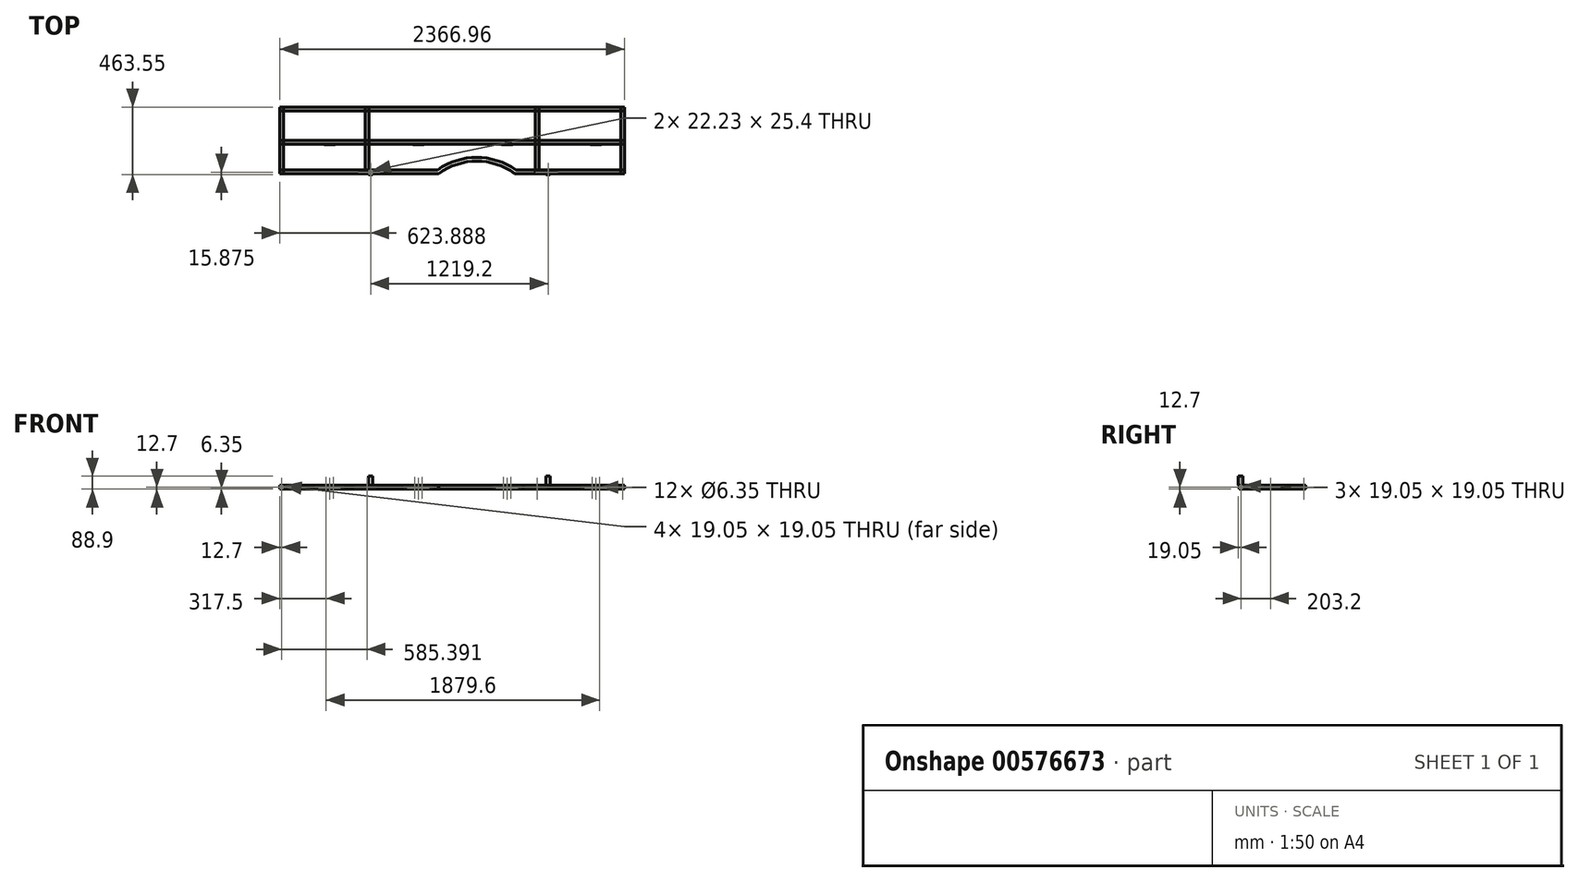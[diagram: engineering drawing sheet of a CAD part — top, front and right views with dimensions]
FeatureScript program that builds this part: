
annotation { "Feature Type Name" : "Feature", "Feature Type Description" : "" }
export const myFeature = defineFeature(function(context is Context, id is Id, definition is map)
    precondition{}
    {
        {
            var Q0;
            Q0=qCreatedBy(makeId("Top.planeOp"),FACE);
            var sketch = newSketch(context, id + "F0", { "sketchPlane" : qUnion([Q0])});
            skLineSegment(sketch, "E0", {"start": v(0, 0) * mm, "end": v(2366.96, 0) * mm});
            skLineSegment(sketch, "E1.0", {"start": v(0, 254) * mm, "end": v(2366.96, 254) * mm});
            skLineSegment(sketch, "E2.0", {"start": v(0, -203.2) * mm, "end": v(1092.2, -203.2) * mm});
            skLineSegment(sketch, "E3", {"start": v(0, 254) * mm, "end": v(0, -203.2) * mm});
            skLineSegment(sketch, "E4", {"start": v(2366.96, 254) * mm, "end": v(2366.96, -203.2) * mm});
            skLineSegment(sketch, "E5.trimOffspring", {"start": v(1612.9, -203.2) * mm, "end": v(2366.96, -203.2) * mm});
            skPoint(sketch, "E6.0.start.orphan", {"position": v(1612.9, 254) * mm});
            skPoint(sketch, "E7.orphan", {"position": v(1092.2, 254) * mm});
            skLineSegment(sketch, "E8", {"start": v(1352.55, -117.48) * mm, "end": v(1352.55, 0) * mm});
            skLineSegment(sketch, "E9.0", {"start": v(0, -117.48) * mm, "end": v(2366.96, -117.48) * mm});
            skPoint(sketch, "E10", {"position": v(1352.55, -117.48) * mm});
            skArc(sketch, "E11", {"start": v(1612.9, -203.2) * mm, "mid": v(1352.55, -117.47) * mm, "end": v(1092.2, -203.2) * mm});
            skLineSegment(sketch, "E12.0", {"start": v(279.4, 254) * mm, "end": v(279.4, -203.2) * mm, "construction": true});
            skLineSegment(sketch, "E13.0", {"start": v(711.2, 254) * mm, "end": v(711.2, -203.2) * mm, "construction": true});
            skLineSegment(sketch, "E14.0", {"start": v(1308.1, 254) * mm, "end": v(1308.1, -203.2) * mm, "construction": true});
            skLineSegment(sketch, "E15.0", {"start": v(1905, 254) * mm, "end": v(1905, -203.2) * mm, "construction": true});
            skLineSegment(sketch, "E16.0", {"start": v(2273.3, 254) * mm, "end": v(2273.3, -203.2) * mm, "construction": true});
            skLineSegment(sketch, "E17.bottom", {"start": v(279.4, 254) * mm, "end": v(335.28, 254) * mm});
            skLineSegment(sketch, "E17.top", {"start": v(279.4, 198.12) * mm, "end": v(335.28, 198.12) * mm});
            skLineSegment(sketch, "E17.left", {"start": v(279.4, 254) * mm, "end": v(279.4, 198.12) * mm});
            skLineSegment(sketch, "E17.right", {"start": v(335.28, 254) * mm, "end": v(335.28, 198.12) * mm});
            skLineSegment(sketch, "E18.bottom", {"start": v(711.2, 254) * mm, "end": v(767.08, 254) * mm});
            skLineSegment(sketch, "E18.top", {"start": v(711.2, 198.12) * mm, "end": v(767.08, 198.12) * mm});
            skLineSegment(sketch, "E18.left", {"start": v(711.2, 254) * mm, "end": v(711.2, 198.12) * mm});
            skLineSegment(sketch, "E18.right", {"start": v(767.08, 254) * mm, "end": v(767.08, 198.12) * mm});
            skLineSegment(sketch, "E19.bottom", {"start": v(1308.1, 254) * mm, "end": v(1363.98, 254) * mm});
            skLineSegment(sketch, "E19.top", {"start": v(1308.1, 198.12) * mm, "end": v(1363.98, 198.12) * mm});
            skLineSegment(sketch, "E19.left", {"start": v(1308.1, 254) * mm, "end": v(1308.1, 198.12) * mm});
            skLineSegment(sketch, "E19.right", {"start": v(1363.98, 254) * mm, "end": v(1363.98, 198.12) * mm});
            skLineSegment(sketch, "E20.bottom", {"start": v(1905, 254) * mm, "end": v(1960.88, 254) * mm});
            skLineSegment(sketch, "E20.top", {"start": v(1905, 198.12) * mm, "end": v(1960.88, 198.12) * mm});
            skLineSegment(sketch, "E20.left", {"start": v(1905, 254) * mm, "end": v(1905, 198.12) * mm});
            skLineSegment(sketch, "E20.right", {"start": v(1960.88, 254) * mm, "end": v(1960.88, 198.12) * mm});
            skLineSegment(sketch, "E21.bottom", {"start": v(2273.3, 254) * mm, "end": v(2329.18, 254) * mm});
            skLineSegment(sketch, "E21.top", {"start": v(2273.3, 198.12) * mm, "end": v(2329.18, 198.12) * mm});
            skLineSegment(sketch, "E21.left", {"start": v(2273.3, 254) * mm, "end": v(2273.3, 198.12) * mm});
            skLineSegment(sketch, "E21.right", {"start": v(2329.18, 254) * mm, "end": v(2329.18, 198.12) * mm});
            skLineSegment(sketch, "E22.0", {"start": v(254, 254) * mm, "end": v(254, -203.2) * mm});
            skLineSegment(sketch, "E23.0", {"start": v(698.5, 254) * mm, "end": v(698.5, -203.2) * mm});
            skLineSegment(sketch, "E24.0", {"start": v(1295.4, 254) * mm, "end": v(1295.4, -203.2) * mm});
            skLineSegment(sketch, "E25.0", {"start": v(1898.65, 254) * mm, "end": v(1898.65, -203.2) * mm});
            skLineSegment(sketch, "E26.0", {"start": v(2266.95, 254) * mm, "end": v(2266.95, -203.2) * mm});
            skLineSegment(sketch, "E27.bottom", {"start": v(254, 254) * mm, "end": v(309.88, 254) * mm});
            skLineSegment(sketch, "E27.top", {"start": v(254, 198.12) * mm, "end": v(309.88, 198.12) * mm});
            skLineSegment(sketch, "E27.left", {"start": v(254, 254) * mm, "end": v(254, 198.12) * mm});
            skLineSegment(sketch, "E27.right", {"start": v(309.88, 254) * mm, "end": v(309.88, 198.12) * mm});
            skLineSegment(sketch, "E28.bottom", {"start": v(698.5, 254) * mm, "end": v(749.3, 254) * mm});
            skLineSegment(sketch, "E28.top", {"start": v(698.5, 198.12) * mm, "end": v(749.3, 198.12) * mm});
            skLineSegment(sketch, "E28.left", {"start": v(698.5, 254) * mm, "end": v(698.5, 198.12) * mm});
            skLineSegment(sketch, "E28.right", {"start": v(749.3, 254) * mm, "end": v(749.3, 198.12) * mm});
            skLineSegment(sketch, "E29.bottom", {"start": v(1295.4, 254) * mm, "end": v(1351.28, 254) * mm});
            skLineSegment(sketch, "E29.top", {"start": v(1295.4, 198.12) * mm, "end": v(1351.28, 198.12) * mm});
            skLineSegment(sketch, "E29.left", {"start": v(1295.4, 254) * mm, "end": v(1295.4, 198.12) * mm});
            skLineSegment(sketch, "E29.right", {"start": v(1351.28, 254) * mm, "end": v(1351.28, 198.12) * mm});
            skLineSegment(sketch, "E30.bottom", {"start": v(1898.65, 254) * mm, "end": v(1954.53, 254) * mm});
            skLineSegment(sketch, "E30.top", {"start": v(1898.65, 198.12) * mm, "end": v(1954.53, 198.12) * mm});
            skLineSegment(sketch, "E30.left", {"start": v(1898.65, 254) * mm, "end": v(1898.65, 198.12) * mm});
            skLineSegment(sketch, "E30.right", {"start": v(1954.53, 254) * mm, "end": v(1954.53, 198.12) * mm});
            skLineSegment(sketch, "E31.bottom", {"start": v(2266.95, 254) * mm, "end": v(2322.83, 254) * mm});
            skLineSegment(sketch, "E31.top", {"start": v(2266.95, 198.12) * mm, "end": v(2322.83, 198.12) * mm});
            skLineSegment(sketch, "E31.left", {"start": v(2266.95, 254) * mm, "end": v(2266.95, 198.12) * mm});
            skLineSegment(sketch, "E31.right", {"start": v(2322.83, 254) * mm, "end": v(2322.83, 198.12) * mm});
            skLineSegment(sketch, "E32.0", {"start": v(2341.56, 254) * mm, "end": v(2341.56, -203.2) * mm, "construction": true});
            skSolve(sketch);
        }
        {
            var Q0;
            Q0=qCreatedBy(makeId("Front.planeOp"),FACE);
            cPlane(context, id + "F1", {"entities" : qUnion([Q0]), "cplaneType" : CPlaneType.OFFSET, "offset" : 203.2 * mm, "width" : 152.4 * mm, "height" : 152.4 * mm});
        }
        {
            var Q0;
            Q0=qCreatedBy(id+"F1.planeOp",FACE);
            var sketch = newSketch(context, id + "F2", { "sketchPlane" : qUnion([Q0])});
            skLineSegment(sketch, "E33.0", {"start": v(25.4, 0) * mm, "end": v(25.4, -25.4) * mm});
            skLineSegment(sketch, "E34.bottom", {"start": v(25.4, -25.4) * mm, "end": v(0, -25.4) * mm});
            skLineSegment(sketch, "E34.top", {"start": v(25.4, 0) * mm, "end": v(0, 0) * mm});
            skLineSegment(sketch, "E34.right", {"start": v(0, -25.4) * mm, "end": v(0, 0) * mm});
            skLineSegment(sketch, "E35.direction1", {"start": v(31.75, -31.75) * mm, "end": v(336.55, -31.75) * mm, "construction": true});
            skLineSegment(sketch, "E36.0", {"start": v(22.22, -3.17) * mm, "end": v(3.18, -3.18) * mm});
            skLineSegment(sketch, "E36.1", {"start": v(22.22, -3.17) * mm, "end": v(22.22, -22.23) * mm});
            skLineSegment(sketch, "E36.2", {"start": v(22.22, -22.23) * mm, "end": v(3.17, -22.23) * mm});
            skLineSegment(sketch, "E36.3", {"start": v(3.18, -22.23) * mm, "end": v(3.18, -3.18) * mm});
            skLineSegment(sketch, "E37.direction1", {"start": v(0, -25.4) * mm, "end": v(2366.96, -25.4) * mm, "construction": true});
            skLineSegment(sketch, "E38.direction1", {"start": v(0, -25.4) * mm, "end": v(609.6, -25.4) * mm, "construction": true});
            skLineSegment(sketch, "E39.1.0.0", {"start": v(610.8, -25.4) * mm, "end": v(585.4, -25.4) * mm});
            skLineSegment(sketch, "E39.1.0.1", {"start": v(585.4, -25.4) * mm, "end": v(585.4, 0) * mm});
            skLineSegment(sketch, "E39.1.0.2", {"start": v(588.57, -22.23) * mm, "end": v(588.57, -3.18) * mm});
            skLineSegment(sketch, "E39.1.0.3", {"start": v(610.8, 0) * mm, "end": v(610.8, -25.4) * mm});
            skLineSegment(sketch, "E39.1.0.4", {"start": v(607.62, -22.23) * mm, "end": v(588.57, -22.23) * mm});
            skLineSegment(sketch, "E39.1.0.5", {"start": v(607.62, -3.17) * mm, "end": v(607.62, -22.23) * mm});
            skLineSegment(sketch, "E39.1.0.6", {"start": v(607.62, -3.17) * mm, "end": v(588.57, -3.18) * mm});
            skLineSegment(sketch, "E39.1.0.7", {"start": v(610.8, 0) * mm, "end": v(585.4, 0) * mm});
            skLineSegment(sketch, "E39.2.0.0", {"start": v(1196.18, -25.4) * mm, "end": v(1170.78, -25.4) * mm});
            skLineSegment(sketch, "E39.2.0.1", {"start": v(1170.78, -25.4) * mm, "end": v(1170.78, 0) * mm});
            skLineSegment(sketch, "E39.2.0.2", {"start": v(1173.96, -22.23) * mm, "end": v(1173.96, -3.18) * mm});
            skLineSegment(sketch, "E39.2.0.3", {"start": v(1196.18, 0) * mm, "end": v(1196.18, -25.4) * mm});
            skLineSegment(sketch, "E39.2.0.4", {"start": v(1193, -22.23) * mm, "end": v(1173.96, -22.23) * mm});
            skLineSegment(sketch, "E39.2.0.5", {"start": v(1193, -3.17) * mm, "end": v(1193, -22.23) * mm});
            skLineSegment(sketch, "E39.2.0.6", {"start": v(1193, -3.17) * mm, "end": v(1173.96, -3.18) * mm});
            skLineSegment(sketch, "E39.2.0.7", {"start": v(1196.18, 0) * mm, "end": v(1170.78, 0) * mm});
            skLineSegment(sketch, "E39.3.0.0", {"start": v(1781.57, -25.4) * mm, "end": v(1756.17, -25.4) * mm});
            skLineSegment(sketch, "E39.3.0.1", {"start": v(1756.17, -25.4) * mm, "end": v(1756.17, 0) * mm});
            skLineSegment(sketch, "E39.3.0.2", {"start": v(1759.35, -22.23) * mm, "end": v(1759.35, -3.18) * mm});
            skLineSegment(sketch, "E39.3.0.3", {"start": v(1781.57, 0) * mm, "end": v(1781.57, -25.4) * mm});
            skLineSegment(sketch, "E39.3.0.4", {"start": v(1778.4, -22.23) * mm, "end": v(1759.35, -22.23) * mm});
            skLineSegment(sketch, "E39.3.0.5", {"start": v(1778.4, -3.17) * mm, "end": v(1778.4, -22.23) * mm});
            skLineSegment(sketch, "E39.3.0.6", {"start": v(1778.4, -3.17) * mm, "end": v(1759.35, -3.18) * mm});
            skLineSegment(sketch, "E39.3.0.7", {"start": v(1781.57, 0) * mm, "end": v(1756.17, 0) * mm});
            skLineSegment(sketch, "E39.4.0.0", {"start": v(2366.96, -25.4) * mm, "end": v(2341.56, -25.4) * mm});
            skLineSegment(sketch, "E39.4.0.1", {"start": v(2341.56, -25.4) * mm, "end": v(2341.56, 0) * mm});
            skLineSegment(sketch, "E39.4.0.2", {"start": v(2344.74, -22.23) * mm, "end": v(2344.74, -3.18) * mm});
            skLineSegment(sketch, "E39.4.0.3", {"start": v(2366.96, 0) * mm, "end": v(2366.96, -25.4) * mm});
            skLineSegment(sketch, "E39.4.0.4", {"start": v(2363.79, -22.23) * mm, "end": v(2344.74, -22.23) * mm});
            skLineSegment(sketch, "E39.4.0.5", {"start": v(2363.79, -3.17) * mm, "end": v(2363.79, -22.23) * mm});
            skLineSegment(sketch, "E39.4.0.6", {"start": v(2363.79, -3.17) * mm, "end": v(2344.74, -3.18) * mm});
            skLineSegment(sketch, "E39.4.0.7", {"start": v(2366.96, 0) * mm, "end": v(2341.56, 0) * mm});
            skLineSegment(sketch, "E39.direction1", {"start": v(0, -25.4) * mm, "end": v(585.4, -25.4) * mm, "construction": true});
            skSolve(sketch);
        }
        {
            var Q0;
            Q0=makeQuery(id+"F2.imprint","IMPRINT",FACE,{"disambiguationData":[TD([[makeQuery(id+"F2.imprint","IMPRINT",EDGE,{"derivedFrom":sQuery(id+"F2.wireOp",EDGE,"E33.0")}),-1.0]])]});
            var Q1;
            Q1=makeQuery(id+"F2.imprint","IMPRINT",FACE,{"disambiguationData":[TD([[makeQuery(id+"F2.imprint","IMPRINT",EDGE,{"derivedFrom":sQuery(id+"F2.wireOp",EDGE,"E39.1.0.0")}),-1.0]])]});
            var Q2;
            Q2=makeQuery(id+"F2.imprint","IMPRINT",FACE,{"disambiguationData":[TD([[makeQuery(id+"F2.imprint","IMPRINT",EDGE,{"derivedFrom":sQuery(id+"F2.wireOp",EDGE,"E39.2.0.0")}),-1.0]])]});
            var Q3;
            Q3=makeQuery(id+"F2.imprint","IMPRINT",FACE,{"disambiguationData":[TD([[makeQuery(id+"F2.imprint","IMPRINT",EDGE,{"derivedFrom":sQuery(id+"F2.wireOp",EDGE,"E39.3.0.0")}),-1.0]])]});
            var Q4;
            Q4=makeQuery(id+"F2.imprint","IMPRINT",FACE,{"disambiguationData":[TD([[makeQuery(id+"F2.imprint","IMPRINT",EDGE,{"derivedFrom":sQuery(id+"F2.wireOp",EDGE,"E39.4.0.0")}),-1.0]])]});
            extrude(context, id + "F3", {"entities" : qUnion([Q0, Q1, Q2, Q3, Q4]), "oppositeDirection" : true, "depth" : 457.2 * mm, "offsetDistance" : 25.4 * mm});
        }
        {
            var Q0;
            Q0=qCreatedBy(makeId("Right.planeOp"),FACE);
            cPlane(context, id + "F4", {"entities" : qUnion([Q0]), "cplaneType" : CPlaneType.OFFSET, "offset" : 2366.96 * mm, "width" : 152.4 * mm, "height" : 152.4 * mm});
        }
        {
            var Q0;
            Q0=qCreatedBy(id+"F4.planeOp",FACE);
            var sketch = newSketch(context, id + "F5", { "sketchPlane" : qUnion([Q0])});
            skLineSegment(sketch, "E40.0", {"start": v(25.4, -25.4) * mm, "end": v(25.4, 0) * mm});
            skLineSegment(sketch, "E41.0", {"start": v(0, -25.4) * mm, "end": v(0, 0) * mm});
            skLineSegment(sketch, "E42", {"start": v(0, -25.4) * mm, "end": v(25.4, -25.4) * mm});
            skLineSegment(sketch, "E43", {"start": v(0, 0) * mm, "end": v(25.4, 0) * mm});
            skLineSegment(sketch, "E44.0", {"start": v(3.18, -22.22) * mm, "end": v(3.18, -3.17) * mm});
            skLineSegment(sketch, "E45.0", {"start": v(22.23, -22.22) * mm, "end": v(22.23, -3.17) * mm});
            skLineSegment(sketch, "E46.0", {"start": v(3.18, -3.17) * mm, "end": v(22.23, -3.17) * mm});
            skLineSegment(sketch, "E47.0", {"start": v(3.18, -22.22) * mm, "end": v(22.23, -22.22) * mm});
            skLineSegment(sketch, "E48.0", {"start": v(-203.2, -25.4) * mm, "end": v(-203.2, 0) * mm});
            skLineSegment(sketch, "E49.bottom", {"start": v(-203.2, -25.4) * mm, "end": v(-177.8, -25.4) * mm});
            skLineSegment(sketch, "E49.top", {"start": v(-203.2, 0) * mm, "end": v(-177.8, 0) * mm});
            skLineSegment(sketch, "E49.right", {"start": v(-177.8, -25.4) * mm, "end": v(-177.8, 0) * mm});
            skLineSegment(sketch, "E50.0", {"start": v(-180.97, -22.22) * mm, "end": v(-180.97, -3.18) * mm});
            skLineSegment(sketch, "E50.1", {"start": v(-200.02, -22.22) * mm, "end": v(-180.97, -22.22) * mm});
            skLineSegment(sketch, "E50.2", {"start": v(-200.02, -22.22) * mm, "end": v(-200.02, -3.18) * mm});
            skLineSegment(sketch, "E50.3", {"start": v(-200.02, -3.18) * mm, "end": v(-180.97, -3.18) * mm});
            skLineSegment(sketch, "E51.1.0.0", {"start": v(228.6, -25.4) * mm, "end": v(254, -25.4) * mm});
            skLineSegment(sketch, "E51.1.0.1", {"start": v(231.78, -22.22) * mm, "end": v(250.83, -22.22) * mm});
            skLineSegment(sketch, "E51.1.0.2", {"start": v(231.78, -3.18) * mm, "end": v(250.83, -3.18) * mm});
            skLineSegment(sketch, "E51.1.0.3", {"start": v(228.6, 0) * mm, "end": v(254, 0) * mm});
            skLineSegment(sketch, "E51.1.0.4", {"start": v(231.78, -22.22) * mm, "end": v(231.78, -3.18) * mm});
            skLineSegment(sketch, "E51.1.0.5", {"start": v(228.6, -25.4) * mm, "end": v(228.6, 0) * mm});
            skLineSegment(sketch, "E51.1.0.6", {"start": v(228.6, -25.4) * mm, "end": v(228.6, 0) * mm});
            skLineSegment(sketch, "E51.1.0.7", {"start": v(250.83, -22.22) * mm, "end": v(250.83, -3.18) * mm});
            skLineSegment(sketch, "E51.1.0.8", {"start": v(254, -25.4) * mm, "end": v(254, 0) * mm});
            skLineSegment(sketch, "E51.direction1", {"start": v(-203.2, -25.4) * mm, "end": v(228.6, -25.4) * mm, "construction": true});
            skSolve(sketch);
        }
        {
            var Q0;
            {var subQ4=sQuery(id+"F5.wireOp",EDGE,"E49.bottom");Q0=makeQuery(id+"F5.imprint","IMPRINT",FACE,{"disambiguationData":[TD([[makeQuery(id+"F5.imprint","IMPRINT",EDGE,{"derivedFrom":subQ4}),1.0]])]});}
            var Q1;
            Q1=sQuery(id+"F0.wireOp",EDGE,"E5.trimOffspring");
            var Q2;
            Q2=sQuery(id+"F0.wireOp",EDGE,"E11");
            var Q3;
            Q3=sQuery(id+"F0.wireOp",EDGE,"E2.0");
            sweep(context, id + "F6", {"profiles" : qUnion([Q0]), "path" : qUnion([Q1, Q2, Q3])});
        }
        {
            var Q0;
            Q0=makeQuery(id+"F5.imprint","IMPRINT",FACE,{"disambiguationData":[TD([[makeQuery(id+"F5.imprint","IMPRINT",EDGE,{"derivedFrom":sQuery(id+"F5.wireOp",EDGE,"E40.0")}),1.0]])]});
            var Q1;
            {var subQ4=sQuery(id+"F5.wireOp",EDGE,"E51.1.0.0");Q1=makeQuery(id+"F5.imprint","IMPRINT",FACE,{"disambiguationData":[TD([[makeQuery(id+"F5.imprint","IMPRINT",EDGE,{"derivedFrom":subQ4}),1.0]])]});}
            var Q2;
            Q2=sQuery(id+"F0.wireOp",EDGE,"E0");
            sweep(context, id + "F7", {"profiles" : qUnion([Q0, Q1]), "path" : qUnion([Q2])});
        }
        {
            var Q0;
            Q0=makeQuery(id+"F6.opSweep","SWEPT_BODY",BODY,{"disambiguationData":[OSD([sQuery(id+"F0.wireOp",EDGE,"E2.0"),sQuery(id+"F5.wireOp",EDGE,"E48.0"),sQuery(id+"F5.wireOp",EDGE,"E49.bottom"),sQuery(id+"F5.wireOp",EDGE,"E49.top"),sQuery(id+"F5.wireOp",EDGE,"E49.right"),sQuery(id+"F5.wireOp",EDGE,"E50.0"),sQuery(id+"F5.wireOp",EDGE,"E50.1"),sQuery(id+"F5.wireOp",EDGE,"E50.2"),sQuery(id+"F5.wireOp",EDGE,"E50.3")])]});
            var Q1;
            Q1=makeQuery(id+"F3.opExtrude","SWEPT_BODY",BODY,{"disambiguationData":[OSD([sQuery(id+"F2.wireOp",EDGE,"E39.2.0.0"),sQuery(id+"F2.wireOp",EDGE,"E39.2.0.1"),sQuery(id+"F2.wireOp",EDGE,"E39.2.0.2"),sQuery(id+"F2.wireOp",EDGE,"E39.2.0.3"),sQuery(id+"F2.wireOp",EDGE,"E39.2.0.4"),sQuery(id+"F2.wireOp",EDGE,"E39.2.0.5"),sQuery(id+"F2.wireOp",EDGE,"E39.2.0.6"),sQuery(id+"F2.wireOp",EDGE,"E39.2.0.7")])]});
            booleanBodies(context, id + "F8", {"operationType" : BooleanOperationType.SUBTRACTION, "tools" : qUnion([Q0]), "targets" : qUnion([Q1]), "keepTools" : true});
        }
        {
            var Q0;
            Q0=makeQuery(id+"F8.opBoolean","SPLIT",BODY,{"disambiguationData":[OD(0.0)],"derivedFrom":makeQuery(id+"F3.opExtrude","SWEPT_BODY",BODY,{"disambiguationData":[OSD([sQuery(id+"F2.wireOp",EDGE,"E38.2.0.0"),sQuery(id+"F2.wireOp",EDGE,"E38.2.0.1"),sQuery(id+"F2.wireOp",EDGE,"E38.2.0.2"),sQuery(id+"F2.wireOp",EDGE,"E38.2.0.3"),sQuery(id+"F2.wireOp",EDGE,"E38.2.0.4"),sQuery(id+"F2.wireOp",EDGE,"E38.2.0.5"),sQuery(id+"F2.wireOp",EDGE,"E38.2.0.6"),sQuery(id+"F2.wireOp",EDGE,"E38.2.0.7")])]})});
            var Q1;
            Q1=makeQuery(id+"F8.opBoolean","SPLIT",BODY,{"disambiguationData":[OD(0.0)],"derivedFrom":makeQuery(id+"F3.opExtrude","SWEPT_BODY",BODY,{"disambiguationData":[OSD([sQuery(id+"F2.wireOp",EDGE,"E39.2.0.0"),sQuery(id+"F2.wireOp",EDGE,"E39.2.0.1"),sQuery(id+"F2.wireOp",EDGE,"E39.2.0.2"),sQuery(id+"F2.wireOp",EDGE,"E39.2.0.3"),sQuery(id+"F2.wireOp",EDGE,"E39.2.0.4"),sQuery(id+"F2.wireOp",EDGE,"E39.2.0.5"),sQuery(id+"F2.wireOp",EDGE,"E39.2.0.6"),sQuery(id+"F2.wireOp",EDGE,"E39.2.0.7")])]})});
            deleteBodies(context, id + "F9", {"entities" : qUnion([Q0, Q1])});
        }
        {
            var Q0;
            Q0=qCreatedBy(makeId("Top.planeOp"),FACE);
            cPlane(context, id + "F10", {"entities" : qUnion([Q0]), "cplaneType" : CPlaneType.OFFSET, "offset" : 0 * mm, "width" : 152.4 * mm, "height" : 152.4 * mm});
        }
        {
            var Q0;
            Q0=qCreatedBy(id+"F10.planeOp",FACE);
            var sketch = newSketch(context, id + "F11", { "sketchPlane" : qUnion([Q0])});
            skLineSegment(sketch, "E52.bottom", {"start": v(0, 0) * mm, "end": v(641.35, 0) * mm});
            skLineSegment(sketch, "E53.bottom", {"start": v(609.6, -177.8) * mm, "end": v(638.17, -177.8) * mm});
            skLineSegment(sketch, "E53.top", {"start": v(609.6, -209.55) * mm, "end": v(638.17, -209.55) * mm});
            skLineSegment(sketch, "E53.left", {"start": v(609.6, -177.8) * mm, "end": v(609.6, -209.55) * mm});
            skLineSegment(sketch, "E53.right", {"start": v(638.17, -177.8) * mm, "end": v(638.17, -209.55) * mm});
            skLineSegment(sketch, "E54.0", {"start": v(612.78, -206.38) * mm, "end": v(635, -206.38) * mm});
            skLineSegment(sketch, "E54.1", {"start": v(612.78, -180.98) * mm, "end": v(612.78, -206.38) * mm});
            skLineSegment(sketch, "E54.2", {"start": v(612.78, -180.98) * mm, "end": v(635, -180.98) * mm});
            skLineSegment(sketch, "E54.3", {"start": v(635, -180.98) * mm, "end": v(635, -206.38) * mm});
            skLineSegment(sketch, "E55.1.0.0", {"start": v(1854.2, -180.98) * mm, "end": v(1854.2, -206.38) * mm});
            skLineSegment(sketch, "E55.1.0.1", {"start": v(1857.37, -177.8) * mm, "end": v(1857.37, -209.55) * mm});
            skLineSegment(sketch, "E55.1.0.2", {"start": v(1831.98, -180.98) * mm, "end": v(1831.98, -206.38) * mm});
            skLineSegment(sketch, "E55.1.0.3", {"start": v(1831.98, -180.98) * mm, "end": v(1854.2, -180.98) * mm});
            skLineSegment(sketch, "E55.1.0.4", {"start": v(1828.8, -177.8) * mm, "end": v(1857.37, -177.8) * mm});
            skLineSegment(sketch, "E55.1.0.5", {"start": v(1828.8, -177.8) * mm, "end": v(1828.8, -209.55) * mm});
            skLineSegment(sketch, "E55.1.0.6", {"start": v(1831.98, -206.38) * mm, "end": v(1854.2, -206.38) * mm});
            skLineSegment(sketch, "E55.1.0.7", {"start": v(1828.8, -209.55) * mm, "end": v(1857.37, -209.55) * mm});
            skLineSegment(sketch, "E55.direction1", {"start": v(609.6, -209.55) * mm, "end": v(1828.8, -209.55) * mm, "construction": true});
            skSolve(sketch);
        }
        {
            var Q0;
            Q0=makeQuery(id+"F11.imprint","IMPRINT",FACE,{"disambiguationData":[TD([[makeQuery(id+"F11.imprint","IMPRINT",EDGE,{"derivedFrom":sQuery(id+"F11.wireOp",EDGE,"E53.bottom")}),-1.0]])]});
            var Q1;
            Q1=makeQuery(id+"F11.imprint","IMPRINT",FACE,{"disambiguationData":[TD([[makeQuery(id+"F11.imprint","IMPRINT",EDGE,{"derivedFrom":sQuery(id+"F11.wireOp",EDGE,"E55.1.0.0")}),1.0]])]});
            extrude(context, id + "F12", {"entities" : qUnion([Q0, Q1]), "depth" : 63.5 * mm, "offsetDistance" : 25.4 * mm});
        }
        {
            var Q0;
            Q0=qCreatedBy(makeId("Front.planeOp"),FACE);
            var sketch = newSketch(context, id + "F13", { "sketchPlane" : qUnion([Q0])});
            skLineSegment(sketch, "E56.bottom", {"start": v(304.8, 0) * mm, "end": v(381, 0) * mm});
            skLineSegment(sketch, "E56.top", {"start": v(304.8, -25.4) * mm, "end": v(381, -25.4) * mm});
            skLineSegment(sketch, "E56.left", {"start": v(304.8, 0) * mm, "end": v(304.8, -25.4) * mm});
            skLineSegment(sketch, "E56.right", {"start": v(381, 0) * mm, "end": v(381, -25.4) * mm});
            skLineSegment(sketch, "E57.0", {"start": v(317.5, -12.7) * mm, "end": v(317.5, -12.7) * mm});
            skLineSegment(sketch, "E57.2", {"start": v(368.3, -12.7) * mm, "end": v(368.3, -12.7) * mm});
            skCircle(sketch, "E58", {"center": v(317.5, -12.7) * mm, "radius": 3.18 * mm});
            skCircle(sketch, "E59", {"center": v(342.9, -19.05) * mm, "radius": 3.18 * mm});
            skCircle(sketch, "E60", {"center": v(368.3, -12.7) * mm, "radius": 3.18 * mm});
            skLineSegment(sketch, "E61.1.0.0", {"start": v(914.4, 0) * mm, "end": v(990.6, 0) * mm});
            skLineSegment(sketch, "E61.1.0.1", {"start": v(914.4, -25.4) * mm, "end": v(990.6, -25.4) * mm});
            skLineSegment(sketch, "E61.1.0.2", {"start": v(914.4, 0) * mm, "end": v(914.4, -25.4) * mm});
            skLineSegment(sketch, "E61.1.0.3", {"start": v(990.6, 0) * mm, "end": v(990.6, -25.4) * mm});
            skCircle(sketch, "E61.1.0.4", {"center": v(952.5, -19.05) * mm, "radius": 3.18 * mm});
            skCircle(sketch, "E61.1.0.5", {"center": v(927.1, -12.7) * mm, "radius": 3.18 * mm});
            skCircle(sketch, "E61.1.0.6", {"center": v(977.9, -12.7) * mm, "radius": 3.18 * mm});
            skLineSegment(sketch, "E61.2.0.0", {"start": v(1524, 0) * mm, "end": v(1600.2, 0) * mm});
            skLineSegment(sketch, "E61.2.0.1", {"start": v(1524, -25.4) * mm, "end": v(1600.2, -25.4) * mm});
            skLineSegment(sketch, "E61.2.0.2", {"start": v(1524, 0) * mm, "end": v(1524, -25.4) * mm});
            skLineSegment(sketch, "E61.2.0.3", {"start": v(1600.2, 0) * mm, "end": v(1600.2, -25.4) * mm});
            skCircle(sketch, "E61.2.0.4", {"center": v(1562.1, -19.05) * mm, "radius": 3.18 * mm});
            skCircle(sketch, "E61.2.0.5", {"center": v(1536.7, -12.7) * mm, "radius": 3.18 * mm});
            skCircle(sketch, "E61.2.0.6", {"center": v(1587.5, -12.7) * mm, "radius": 3.18 * mm});
            skLineSegment(sketch, "E61.3.0.0", {"start": v(2133.6, 0) * mm, "end": v(2209.8, 0) * mm});
            skLineSegment(sketch, "E61.3.0.1", {"start": v(2133.6, -25.4) * mm, "end": v(2209.8, -25.4) * mm});
            skLineSegment(sketch, "E61.3.0.2", {"start": v(2133.6, 0) * mm, "end": v(2133.6, -25.4) * mm});
            skLineSegment(sketch, "E61.3.0.3", {"start": v(2209.8, 0) * mm, "end": v(2209.8, -25.4) * mm});
            skCircle(sketch, "E61.3.0.4", {"center": v(2171.7, -19.05) * mm, "radius": 3.18 * mm});
            skCircle(sketch, "E61.3.0.5", {"center": v(2146.3, -12.7) * mm, "radius": 3.18 * mm});
            skCircle(sketch, "E61.3.0.6", {"center": v(2197.1, -12.7) * mm, "radius": 3.18 * mm});
            skLineSegment(sketch, "E61.direction1", {"start": v(304.8, -25.4) * mm, "end": v(914.4, -25.4) * mm, "construction": true});
            skSolve(sketch);
        }
        {
            var Q0;
            Q0=makeQuery(id+"F13.imprint","IMPRINT",FACE,{"disambiguationData":[TD([[makeQuery(id+"F13.imprint","IMPRINT",EDGE,{"derivedFrom":sQuery(id+"F13.wireOp",EDGE,"E56.bottom")}),-1.0]])]});
            var Q1;
            Q1=makeQuery(id+"F13.imprint","IMPRINT",FACE,{"disambiguationData":[TD([[makeQuery(id+"F13.imprint","IMPRINT",EDGE,{"derivedFrom":sQuery(id+"F13.wireOp",EDGE,"E61.1.0.0")}),-1.0]])]});
            var Q2;
            Q2=makeQuery(id+"F13.imprint","IMPRINT",FACE,{"disambiguationData":[TD([[makeQuery(id+"F13.imprint","IMPRINT",EDGE,{"derivedFrom":sQuery(id+"F13.wireOp",EDGE,"E61.2.0.0")}),-1.0]])]});
            var Q3;
            Q3=makeQuery(id+"F13.imprint","IMPRINT",FACE,{"disambiguationData":[TD([[makeQuery(id+"F13.imprint","IMPRINT",EDGE,{"derivedFrom":sQuery(id+"F13.wireOp",EDGE,"E61.3.0.0")}),-1.0]])]});
            extrude(context, id + "F14", {"entities" : qUnion([Q0, Q1, Q2, Q3]), "depth" : 3.17 * mm, "offsetDistance" : 25.4 * mm});
        }
        {
            var Q0;
            Q0=qCreatedBy(id+"F10.planeOp",FACE);
            cPlane(context, id + "F15", {"entities" : qUnion([Q0]), "cplaneType" : CPlaneType.OFFSET, "offset" : 50.8 * mm, "width" : 152.4 * mm, "height" : 152.4 * mm});
        }
    });
